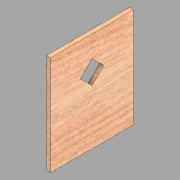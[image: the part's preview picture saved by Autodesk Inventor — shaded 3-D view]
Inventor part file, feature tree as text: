
AUTODESK INVENTOR PART (.ipt)
format: ipt  version: 2020 (Build 240168000, 168)  size: 116,736 bytes
history: native  units: in
note: dims shown in document units (in); Inventor stores cm internally (conversion verified against a paired STEP export)
features: extrude x2, sketch x2
ambient origin geometry x8: Origin, YZ Plane, XZ Plane, XY Plane, X Axis, Y Axis, Z Axis, Center Point
bodies: Solid1 (feature_tree)
feature tree (4):
  extrude  "Extrusion1"  Depth=6.0in
  extrude  "Extrusion2"  Depth=1.0in
  sketch  "Sketch1"  dims[d0=0.25in d1=6.0in]
  sketch  "Sketch2"  dims[d2=5.0in d3=0.0in d4=1.0in d5=45.0deg d6=1.0in d7=2.0in d8=5.0in d9=0.0in]
